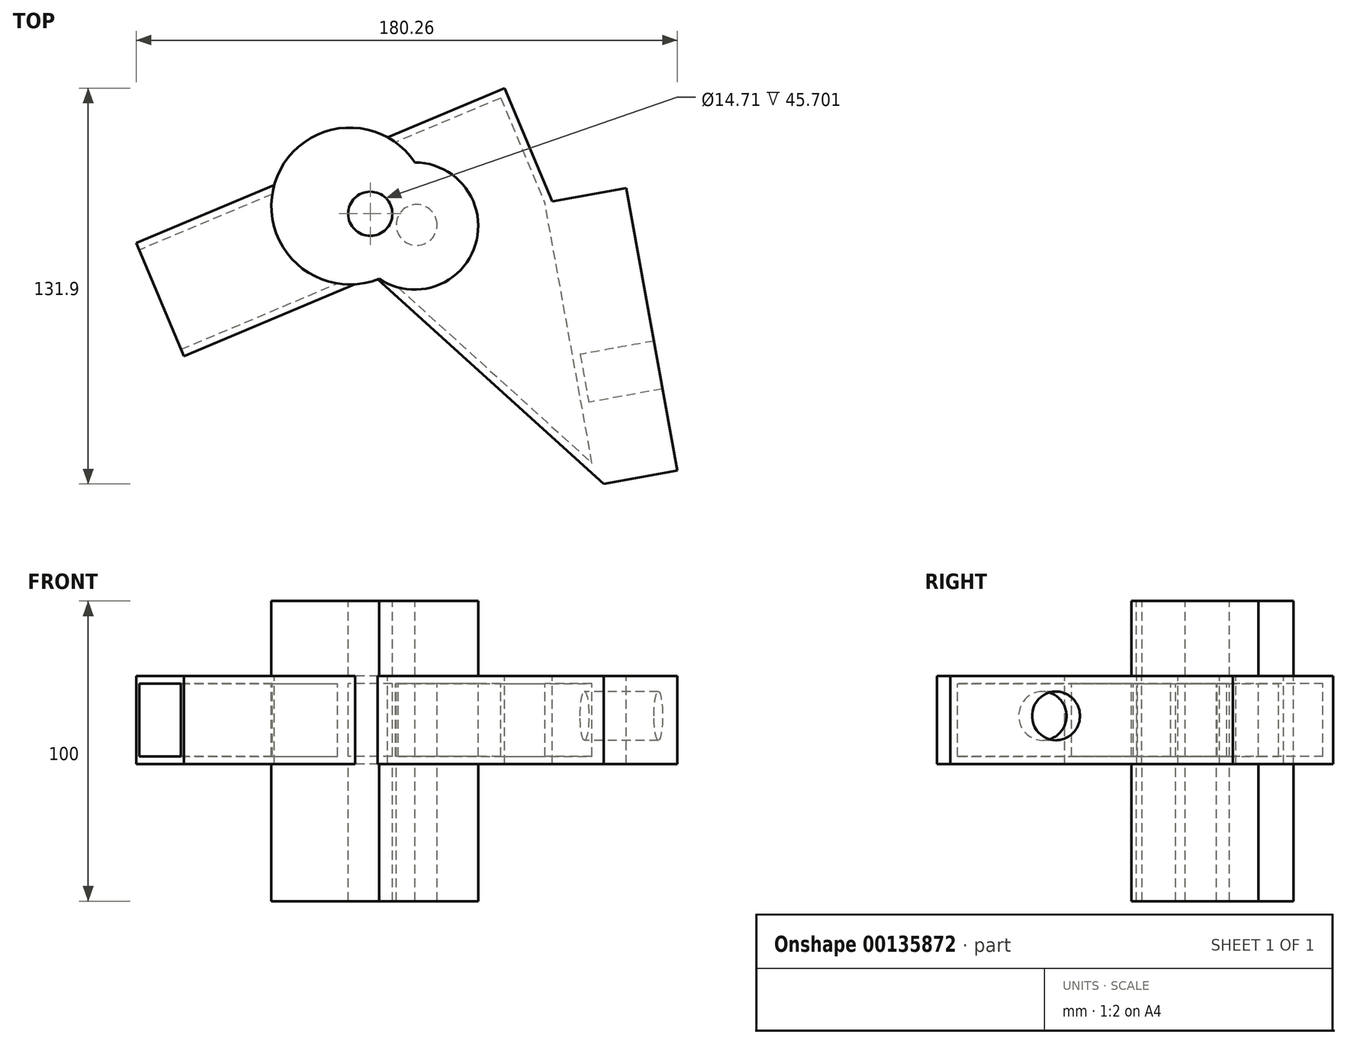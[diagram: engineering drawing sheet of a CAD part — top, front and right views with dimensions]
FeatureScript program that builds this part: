
annotation { "Feature Type Name" : "Feature", "Feature Type Description" : "" }
export const myFeature = defineFeature(function(context is Context, id is Id, definition is map)
    precondition{}
    {
        {
            var Q0;
            Q0=qCreatedBy(makeId("Top.planeOp"),FACE);
            var sketch = newSketch(context, id + "F0", { "sketchPlane" : qUnion([Q0])});
            skLineSegment(sketch, "E0", {"start": v(0, 34.08) * mm, "end": v(-59.28, 9.13) * mm});
            skLineSegment(sketch, "E1", {"start": v(-59.28, 9.13) * mm, "end": v(17.05, -60.07) * mm});
            skLineSegment(sketch, "E2", {"start": v(17.05, -60.07) * mm, "end": v(0, 34.08) * mm});
            skPoint(sketch, "E3.0", {"position": v(0, 0) * mm});
            skSolve(sketch);
        }
        {
            var Q0;
            Q0=makeQuery(id+"F0.imprint","IMPRINT",FACE,{"disambiguationData":[TD([[makeQuery(id+"F0.imprint","IMPRINT",EDGE,{"derivedFrom":sQuery(id+"F0.wireOp",EDGE,"E0")}),1.0]])]});
            extrude(context, id + "F1", {"entities" : qUnion([Q0]), "oppositeDirection" : true, "depth" : 29.3 * mm});
        }
        {
            var Q0;
            Q0=makeQuery(id+"F1.opExtrude","SWEPT_FACE",FACE,{"disambiguationData":[OSD([sQuery(id+"F0.wireOp",EDGE,"E0")])]});
            extrude(context, id + "F2", {"entities" : qUnion([Q0]), "operationType" : NewBodyOperationType.ADD, "depth" : 40.96 * mm});
        }
        {
            var Q0;
            Q0=makeQuery(id+"F2.opExtrude","SWEPT_FACE",FACE,{"disambiguationData":[OSD([sQuery(id+"F0.wireOp",EDGE,"E0"),sQuery(id+"F0.wireOp",EDGE,"E1")])]});
            extrude(context, id + "F3", {"entities" : qUnion([Q0]), "operationType" : NewBodyOperationType.ADD, "depth" : 68.83 * mm});
        }
        {
            var Q0;
            Q0=makeQuery(id+"F3.opExtrude","CAP_FACE",FACE,{"disambiguationData":[OSD([sQuery(id+"F0.wireOp",EDGE,"E0"),sQuery(id+"F0.wireOp",EDGE,"E1")])],"isStart":false});
            shell(context, id + "F4", {"entities" : qUnion([Q0]), "thickness" : 2.54 * mm});
        }
        {
            var Q0;
            Q0=makeQuery(id+"F1.opExtrude","SWEPT_FACE",FACE,{"disambiguationData":[OSD([sQuery(id+"F0.wireOp",EDGE,"E2")])]});
            var sketch = newSketch(context, id + "F5", { "sketchPlane" : qUnion([Q0])});
            skCircle(sketch, "E4", {"center": v(-26.38, -13.29) * mm, "radius": 8.1 * mm});
            skSolve(sketch);
        }
        {
            var Q0;
            Q0=makeQuery(id+"F5.imprint","IMPRINT",FACE,{"disambiguationData":[TD([[makeQuery(id+"F5.imprint","IMPRINT",EDGE,{"derivedFrom":sQuery(id+"F5.wireOp",EDGE,"E4")}),-1.0]])]});
            extrude(context, id + "F6", {"entities" : qUnion([Q0]), "operationType" : NewBodyOperationType.ADD, "depth" : 25 * mm});
        }
        {
            var Q0;
            {var subQ0=sQuery(id+"F0.wireOp",EDGE,"E2");var subQ1=sQuery(id+"F0.wireOp",EDGE,"E1");var subQ2=sQuery(id+"F0.wireOp",EDGE,"E0");Q0=makeQuery(id+"F6.boolean.opBoolean","MERGE",FACE,{"derivedFrom":[makeQuery(id+"F3.boolean.opBoolean","MERGE",FACE,{"derivedFrom":[makeQuery(id+"F2.boolean.opBoolean","MERGE",FACE,{"derivedFrom":[makeQuery(id+"F1.opExtrude","CAP_FACE",FACE,{"disambiguationData":[OSD([subQ2,subQ1,subQ0])],"isStart":true}),makeQuery(id+"F2.opExtrude","SWEPT_FACE",FACE,{"disambiguationData":[OSD([subQ2]),TDD([makeQuery(id+"F1.opExtrude","CAP_EDGE",EDGE,{"disambiguationData":[OSD([subQ2])],"isStart":true})])]})]}),makeQuery(id+"F3.opExtrude","SWEPT_FACE",FACE,{"disambiguationData":[OSD([subQ2,subQ1]),TDD([makeQuery(id+"F2.opExtrude","SWEPT_EDGE",EDGE,{"disambiguationData":[OSD([subQ2,subQ1]),TDD([makeQuery(id+"F1.opExtrude","CAP_VERTEX",VERTEX,{"disambiguationData":[OSD([subQ2,subQ1])],"isStart":true})])]})])]})]}),makeQuery(id+"F6.opExtrude","SWEPT_FACE",FACE,{"disambiguationData":[OSD([subQ0]),TDD([makeQuery(id+"F5.imprint","IMPRINT",EDGE,{"derivedFrom":makeQuery(id+"F1.opExtrude","CAP_EDGE",EDGE,{"disambiguationData":[OSD([subQ0])],"isStart":true})})])]})]});}
            var sketch = newSketch(context, id + "F7", { "sketchPlane" : qUnion([Q0])});
            skCircle(sketch, "E5", {"center": v(-45.21, 26.22) * mm, "radius": 8.52 * mm});
            skSolve(sketch);
        }
        {
            var Q0;
            Q0 = qSketchRegion(id + "F7", true);
            extrude(context, id + "F8", {"entities" : qUnion([Q0]), "operationType" : NewBodyOperationType.ADD, "depth" : 25 * mm});
        }
        {
            var Q0;
            Q0=makeQuery(id+"F8.opExtrude","CAP_FACE",FACE,{"disambiguationData":[OSD([sQuery(id+"F7.wireOp",EDGE,"E5")])],"isStart":false});
            var sketch = newSketch(context, id + "F9", { "sketchPlane" : qUnion([Q0])});
            skCircle(sketch, "E6", {"center": v(-60.65, 29.94) * mm, "radius": 7.35 * mm});
            skCircle(sketch, "E7", {"center": v(-45.21, 26.22) * mm, "radius": 6.8 * mm});
            skCircle(sketch, "E8", {"center": v(-45.9, 25.86) * mm, "radius": 21.2 * mm});
            skCircle(sketch, "E9", {"center": v(-67.49, 32.5) * mm, "radius": 26.12 * mm});
            skSolve(sketch);
        }
        {
            var Q0;
            Q0 = qSketchRegion(id + "F9", true);
            extrude(context, id + "F10", {"entities" : qUnion([Q0]), "operationType" : NewBodyOperationType.ADD, "oppositeDirection" : true, "depth" : 100 * mm});
        }
    });
